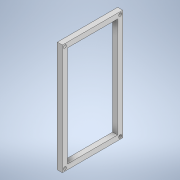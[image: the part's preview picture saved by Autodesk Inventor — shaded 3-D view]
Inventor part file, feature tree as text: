
AUTODESK INVENTOR PART (.ipt)
format: ipt  version: 2021 (Build 250183000, 183)  size: 117,248 bytes
history: native  units: mm
features: extrude x1, sketch x1
ambient origin geometry x8: Origin, YZ Plane, XZ Plane, XY Plane, X Axis, Y Axis, Z Axis, Center Point
bodies: Solide1 (feature_tree)
feature tree (2):
  extrude  "Extrusion1"  Depth=10.0mm
  sketch  "Esquisse1"
